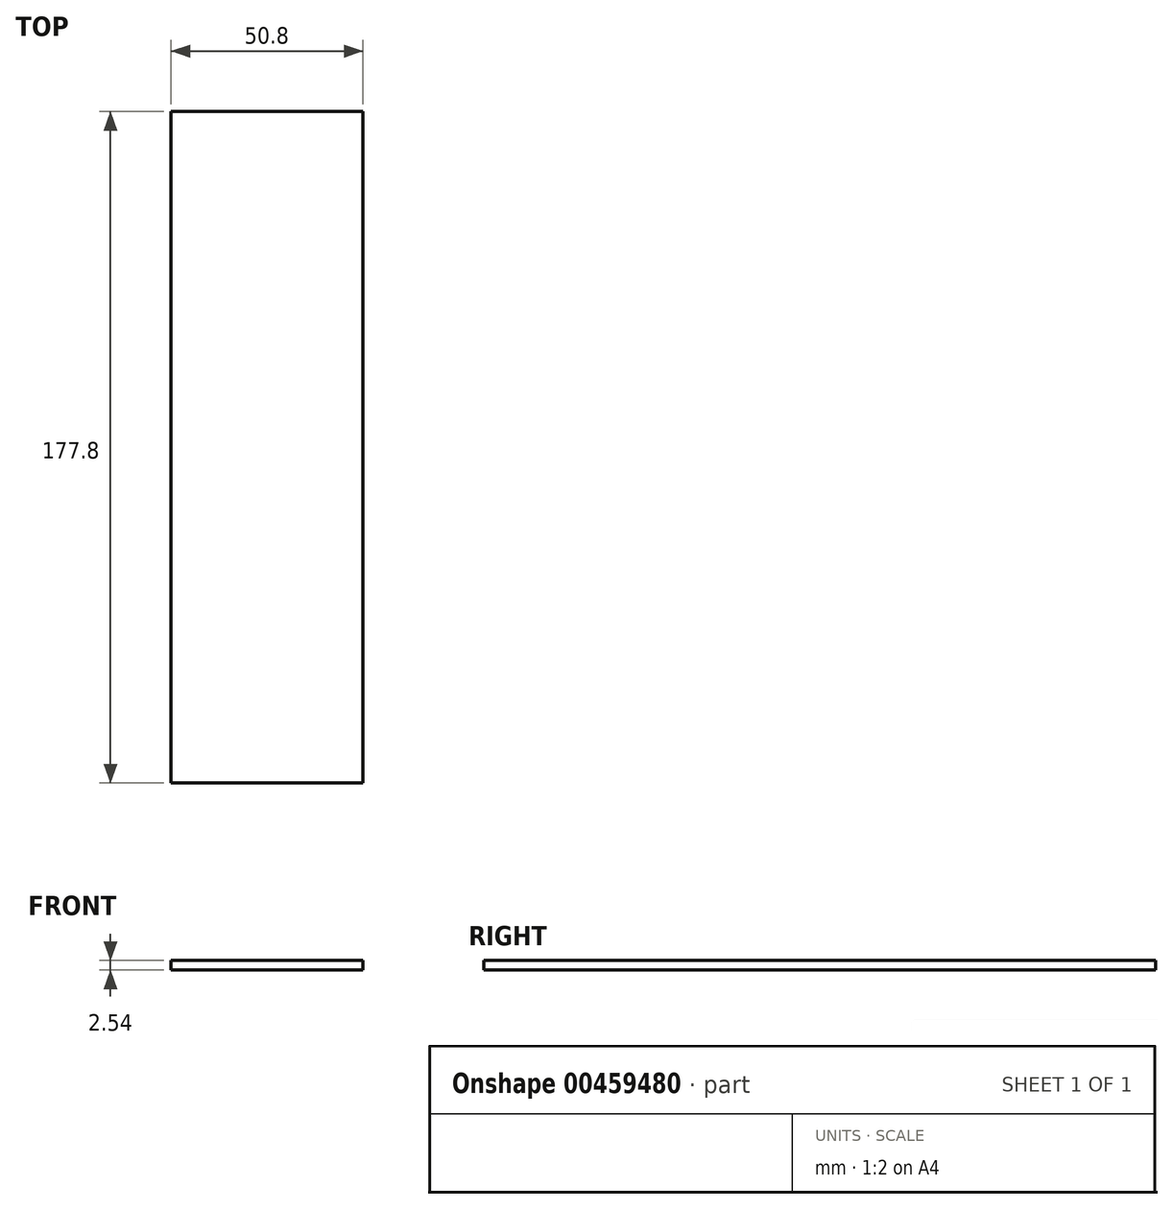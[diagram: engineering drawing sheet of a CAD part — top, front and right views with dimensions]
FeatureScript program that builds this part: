
annotation { "Feature Type Name" : "Feature", "Feature Type Description" : "" }
export const myFeature = defineFeature(function(context is Context, id is Id, definition is map)
    precondition{}
    {
        {
            var Q0;
            Q0=qCreatedBy(makeId("Right.planeOp"),FACE);
            var sketch = newSketch(context, id + "F0", { "sketchPlane" : qUnion([Q0])});
            skLineSegment(sketch, "E0", {"start": v(99.05, 2.54) * mm, "end": v(-78.75, 2.54) * mm});
            skLineSegment(sketch, "E1", {"start": v(-78.75, 2.54) * mm, "end": v(-78.75, 0) * mm});
            skLineSegment(sketch, "E2", {"start": v(-78.75, 0) * mm, "end": v(99.05, 0) * mm});
            skLineSegment(sketch, "E3", {"start": v(99.05, 0) * mm, "end": v(99.05, 2.54) * mm});
            skSolve(sketch);
        }
        {
            var Q0;
            Q0=makeQuery(id+"F0.imprint","IMPRINT",FACE,{"disambiguationData":[TD([[makeQuery(id+"F0.imprint","IMPRINT",EDGE,{"derivedFrom":sQuery(id+"F0.wireOp",EDGE,"E0")}),1.0]])]});
            extrude(context, id + "F1", {"entities" : qUnion([Q0]), "oppositeDirection" : true, "depth" : 50.8 * mm});
        }
    });
